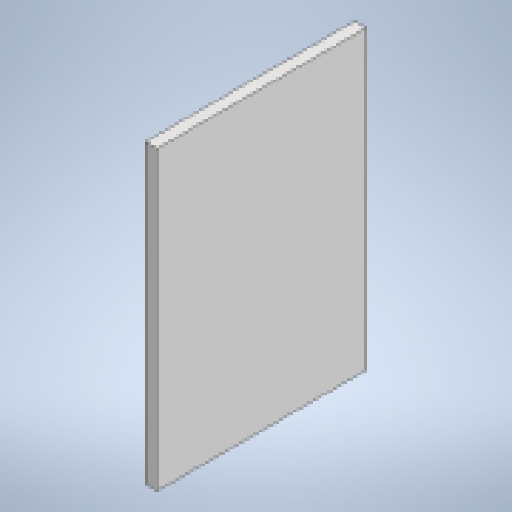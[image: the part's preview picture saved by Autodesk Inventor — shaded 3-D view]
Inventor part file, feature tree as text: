
AUTODESK INVENTOR PART (.ipt)
format: ipt  version: 2023 (Build 270158000, 158)  size: 136,704 bytes
history: native  units: in
note: dims shown in document units (in); Inventor stores cm internally (conversion verified against a paired STEP export)
features: extrude x2, sketch x2
ambient origin geometry x8: Origin, YZ Plane, XZ Plane, XY Plane, X Axis, Y Axis, Z Axis, Center Point
bodies: Solid1 (feature_tree)
feature tree (4):
  extrude  "Extrusion1"  Depth=8.5in
  extrude  "Extrusion2"  Depth=0.3333in
  sketch  "Sketch1"  dims[d0=6.0in d1=8.5in]
  sketch  "Sketch3"  dims[d2=0.3333in d3=0.0in d4=0.315in d5=0.9843in d6=3.5433in d7=0.5906in d8=0.3333in d9=0.0in]
